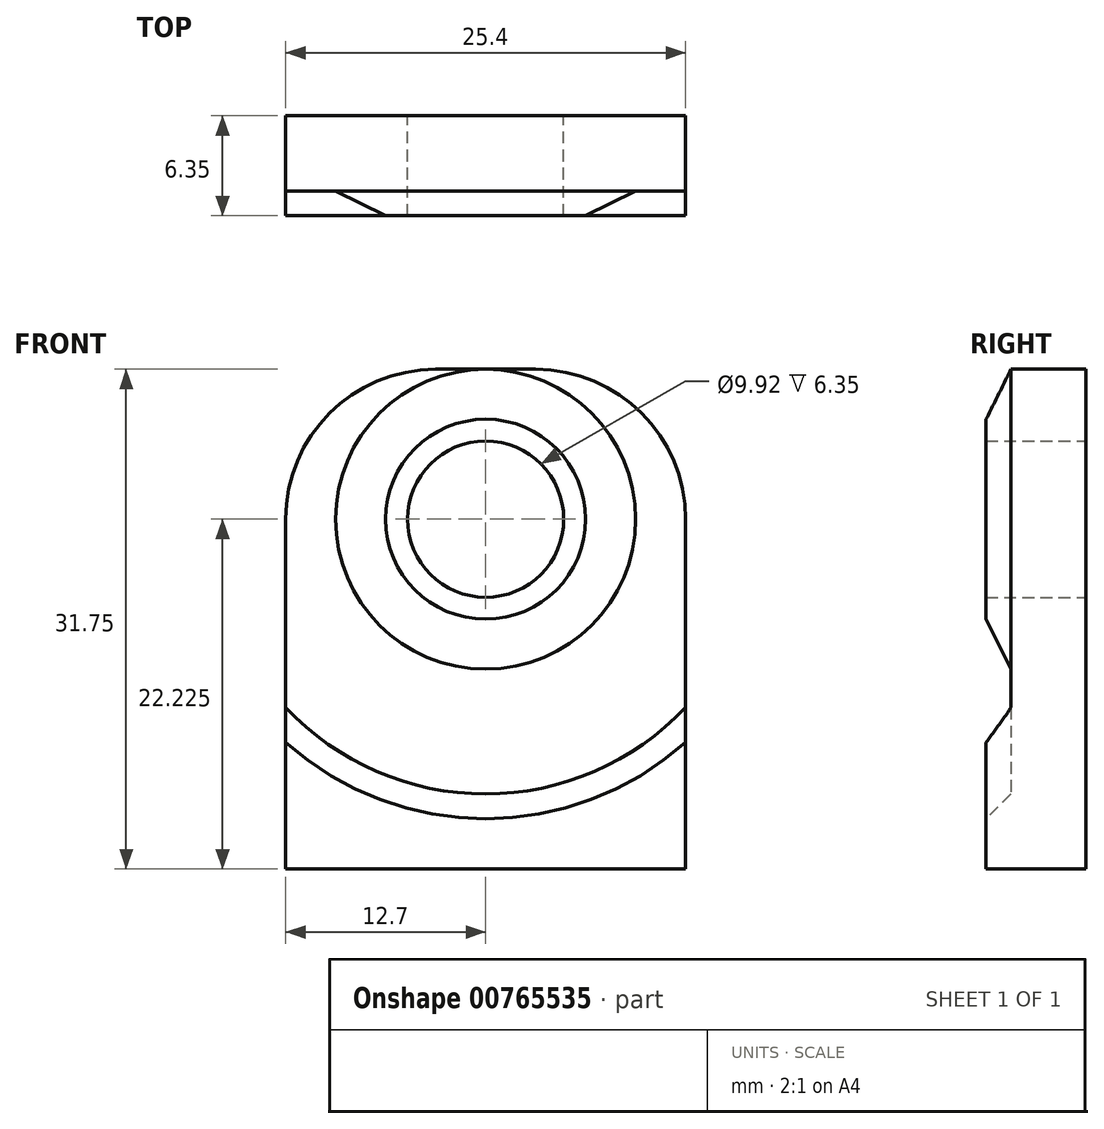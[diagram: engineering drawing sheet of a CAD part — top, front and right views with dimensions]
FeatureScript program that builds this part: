
annotation { "Feature Type Name" : "Feature", "Feature Type Description" : "" }
export const myFeature = defineFeature(function(context is Context, id is Id, definition is map)
    precondition{}
    {
        {
            var Q0;
            Q0=qCreatedBy(makeId("Front.planeOp"),FACE);
            var sketch = newSketch(context, id + "F0", { "sketchPlane" : qUnion([Q0])});
            skLineSegment(sketch, "E0.bottom", {"start": v(0, 0) * mm, "end": v(25.4, 0) * mm});
            skLineSegment(sketch, "E0.top", {"start": v(0, 31.75) * mm, "end": v(25.4, 31.75) * mm});
            skLineSegment(sketch, "E0.left", {"start": v(0, 0) * mm, "end": v(0, 31.75) * mm});
            skLineSegment(sketch, "E0.right", {"start": v(25.4, 0) * mm, "end": v(25.4, 31.75) * mm});
            skCircle(sketch, "E1", {"center": v(12.7, 22.23) * mm, "radius": 9.52 * mm});
            skCircle(sketch, "E2", {"center": v(12.7, 22.23) * mm, "radius": 4.95 * mm});
            skSolve(sketch);
        }
        {
            var Q0;
            Q0=makeQuery(id+"F0.imprint","IMPRINT",FACE,{"disambiguationData":[TD([[makeQuery(id+"F0.imprint","IMPRINT",EDGE,{"derivedFrom":sQuery(id+"F0.wireOp",EDGE,"E0.bottom")}),1.0]])]});
            var Q1;
            Q1 = qSketchRegion(id + "F0", true);
            extrude(context, id + "F1", {"entities" : qUnion([Q0, Q1]), "depth" : 4.78 * mm, "offsetDistance" : 25.4 * mm});
        }
        {
            var Q0;
            Q0=makeQuery(id+"F0.imprint","IMPRINT",FACE,{"disambiguationData":[TD([[makeQuery(id+"F0.imprint","IMPRINT",EDGE,{"derivedFrom":sQuery(id+"F0.wireOp",EDGE,"E1")}),1.0]])]});
            var Q1;
            Q1=sQuery(id+"F0.wireOp",EDGE,"E1");
            var Q2;
            Q2=sQuery(id+"F0.wireOp",EDGE,"E2");
            extrude(context, id + "F2", {"entities" : qUnion([Q0]), "operationType" : NewBodyOperationType.ADD, "surfaceEntities" : qUnion([Q1, Q2]), "depth" : 6.35 * mm, "offsetDistance" : 25.4 * mm});
        }
        {
            var Q0;
            Q0=makeQuery(id+"F2.opExtrude","CAP_FACE",FACE,{"disambiguationData":[OSD([sQuery(id+"F0.wireOp",EDGE,"E1"),sQuery(id+"F0.wireOp",EDGE,"E2")])],"isStart":false});
            var sketch = newSketch(context, id + "F3", { "sketchPlane" : qUnion([Q0])});
            skCircle(sketch, "E3.0", {"center": v(12.7, 22.23) * mm, "radius": 9.52 * mm, "construction": true});
            skArc(sketch, "E4", {"start": v(0, 10.26) * mm, "mid": v(12.7, 4.78) * mm, "end": v(25.4, 10.26) * mm});
            skLineSegment(sketch, "E5.0", {"start": v(0, 0) * mm, "end": v(25.4, 0) * mm});
            skPoint(sketch, "E6", {"position": v(12.7, 4.78) * mm});
            skLineSegment(sketch, "E7", {"start": v(0, 0) * mm, "end": v(0, 10.26) * mm});
            skLineSegment(sketch, "E8", {"start": v(25.4, 0) * mm, "end": v(25.4, 10.26) * mm});
            skSolve(sketch);
        }
        {
            var Q0;
            Q0 = qSketchRegion(id + "F3", true);
            var Q1;
            Q1=makeQuery(id+"F1.opExtrude","CAP_FACE",FACE,{"disambiguationData":[OSD([sQuery(id+"F0.wireOp",EDGE,"E0.bottom"),sQuery(id+"F0.wireOp",EDGE,"E0.top"),sQuery(id+"F0.wireOp",EDGE,"E0.left"),sQuery(id+"F0.wireOp",EDGE,"E0.right"),sQuery(id+"F0.wireOp",EDGE,"E2")])],"isStart":false});
            var Q2;
            Q2=makeQuery(id+"F1.opExtrude","SWEPT_BODY",BODY,{"disambiguationData":[OSD([sQuery(id+"F0.wireOp",EDGE,"E0.bottom"),sQuery(id+"F0.wireOp",EDGE,"E0.top"),sQuery(id+"F0.wireOp",EDGE,"E0.left"),sQuery(id+"F0.wireOp",EDGE,"E0.right"),sQuery(id+"F0.wireOp",EDGE,"E2")])]});
            extrude(context, id + "F4", {"entities" : qUnion([Q0]), "operationType" : NewBodyOperationType.ADD, "endBound" : BoundingType.UP_TO_NEXT, "oppositeDirection" : true, "depth" : 25.4 * mm, "endBoundEntityFace" : qUnion([Q1]), "endBoundEntityBody" : qUnion([Q2]), "offsetDistance" : 25.4 * mm});
        }
        {
            var Q0;
            Q0=makeQuery(id+"F2.opExtrude","CAP_EDGE",EDGE,{"disambiguationData":[OSD([sQuery(id+"F0.wireOp",EDGE,"E1")])],"isStart":false});
            chamfer(context, id + "F5", {"entities" : qUnion([Q0]), "chamferType" : ChamferType.TWO_OFFSETS, "width1" : 3.17 * mm, "oppositeDirection" : false, "width2" : 1.57 * mm, "tangentPropagation" : true});
        }
        {
            var Q0;
            Q0=makeQuery(id+"F4.opExtrude","CAP_EDGE",EDGE,{"disambiguationData":[OSD([sQuery(id+"F3.wireOp",EDGE,"E4")])],"isStart":true});
            chamfer(context, id + "F6", {"entities" : qUnion([Q0]), "width" : 1.57 * mm, "tangentPropagation" : true});
        }
        {
            var Q0;
            Q0=makeQuery(id+"F1.opExtrude","SWEPT_EDGE",EDGE,{"disambiguationData":[OSD([sQuery(id+"F0.wireOp",EDGE,"E0.top"),sQuery(id+"F0.wireOp",EDGE,"E0.left")])]});
            var Q1;
            Q1=makeQuery(id+"F1.opExtrude","SWEPT_EDGE",EDGE,{"disambiguationData":[OSD([sQuery(id+"F0.wireOp",EDGE,"E0.top"),sQuery(id+"F0.wireOp",EDGE,"E0.right")])]});
            fillet(context, id + "F7", {"entities" : qUnion([Q0, Q1]), "radius" : 9.52 * mm, "tangentPropagation" : true, "allowEdgeOverflow" : false});
        }
        {
            var Q0;
            Q0=makeQuery(id+"F2.opExtrude","CAP_FACE",FACE,{"disambiguationData":[OSD([sQuery(id+"F0.wireOp",EDGE,"E1"),sQuery(id+"F0.wireOp",EDGE,"E2")])],"isStart":false});
            var sketch = newSketch(context, id + "F8", { "sketchPlane" : qUnion([Q0])});
            skCircle(sketch, "E9.0", {"center": v(12.7, 22.23) * mm, "radius": 4.95 * mm});
            skSolve(sketch);
        }
        {
            var Q0;
            Q0 = qSketchRegion(id + "F8", true);
            var Q1;
            Q1=makeQuery(id+"F1.opExtrude","CAP_FACE",FACE,{"disambiguationData":[OSD([sQuery(id+"F0.wireOp",EDGE,"E0.bottom"),sQuery(id+"F0.wireOp",EDGE,"E0.top"),sQuery(id+"F0.wireOp",EDGE,"E0.left"),sQuery(id+"F0.wireOp",EDGE,"E0.right"),sQuery(id+"F0.wireOp",EDGE,"E2")])],"isStart":true});
            extrude(context, id + "F9", {"entities" : qUnion([Q0]), "operationType" : NewBodyOperationType.ADD, "endBound" : BoundingType.UP_TO_SURFACE, "oppositeDirection" : true, "depth" : 25.4 * mm, "endBoundEntityFace" : qUnion([Q1]), "offsetDistance" : 25.4 * mm});
        }
        {
            var Q0;
            Q0=makeQuery(id+"F9.boolean.opBoolean","MERGE",FACE,{"derivedFrom":[makeQuery(id+"F2.opExtrude","CAP_FACE",FACE,{"disambiguationData":[OSD([sQuery(id+"F0.wireOp",EDGE,"E1"),sQuery(id+"F0.wireOp",EDGE,"E2")])],"isStart":false}),makeQuery(id+"F9.opExtrude","CAP_FACE",FACE,{"disambiguationData":[OSD([sQuery(id+"F8.wireOp",EDGE,"E9.0")])],"isStart":true})]});
            var sketch = newSketch(context, id + "F10", { "sketchPlane" : qUnion([Q0])});
            skPoint(sketch, "E10", {"position": v(12.7, 22.23) * mm});
            skSolve(sketch);
        }
        {
            var Q0;
            Q0=sQuery(id+"F10.wireOp",VERTEX,"E10");
            var Q1;
            Q1=makeQuery(id+"F1.opExtrude","SWEPT_BODY",BODY,{"disambiguationData":[OSD([sQuery(id+"F0.wireOp",EDGE,"E0.bottom"),sQuery(id+"F0.wireOp",EDGE,"E0.top"),sQuery(id+"F0.wireOp",EDGE,"E0.left"),sQuery(id+"F0.wireOp",EDGE,"E0.right"),sQuery(id+"F0.wireOp",EDGE,"E2")])]});
            hole(context, id + "F11", {"style" : HoleStyle.SIMPLE, "endStyle" : HoleEndStyle.THROUGH, "standardTappedOrClearance" : lookupTablePath({ "fit" : "Normal (ASME)", "standard" : "ANSI", "engagement" : "75%", "pitch" : "20 tpi", "size" : "7/16", "type" : "Tapped" }), "standardBlindInLast" : lookupTablePath({ "fit" : "Free", "standard" : "ANSI", "engagement" : "75%", "pitch" : "20 tpi", "size" : "7/16", "type" : "Tapped" }), "holeDiameter" : 9.92 * mm, "majorDiameter" : 11.1 * mm, "showTappedDepth" : true, "isTappedThrough" : true, "tappedDepth" : 12.7 * mm, "tapClearance" : 3, "locations" : qUnion([Q0]), "scope" : qUnion([Q1])});
        }
    });
